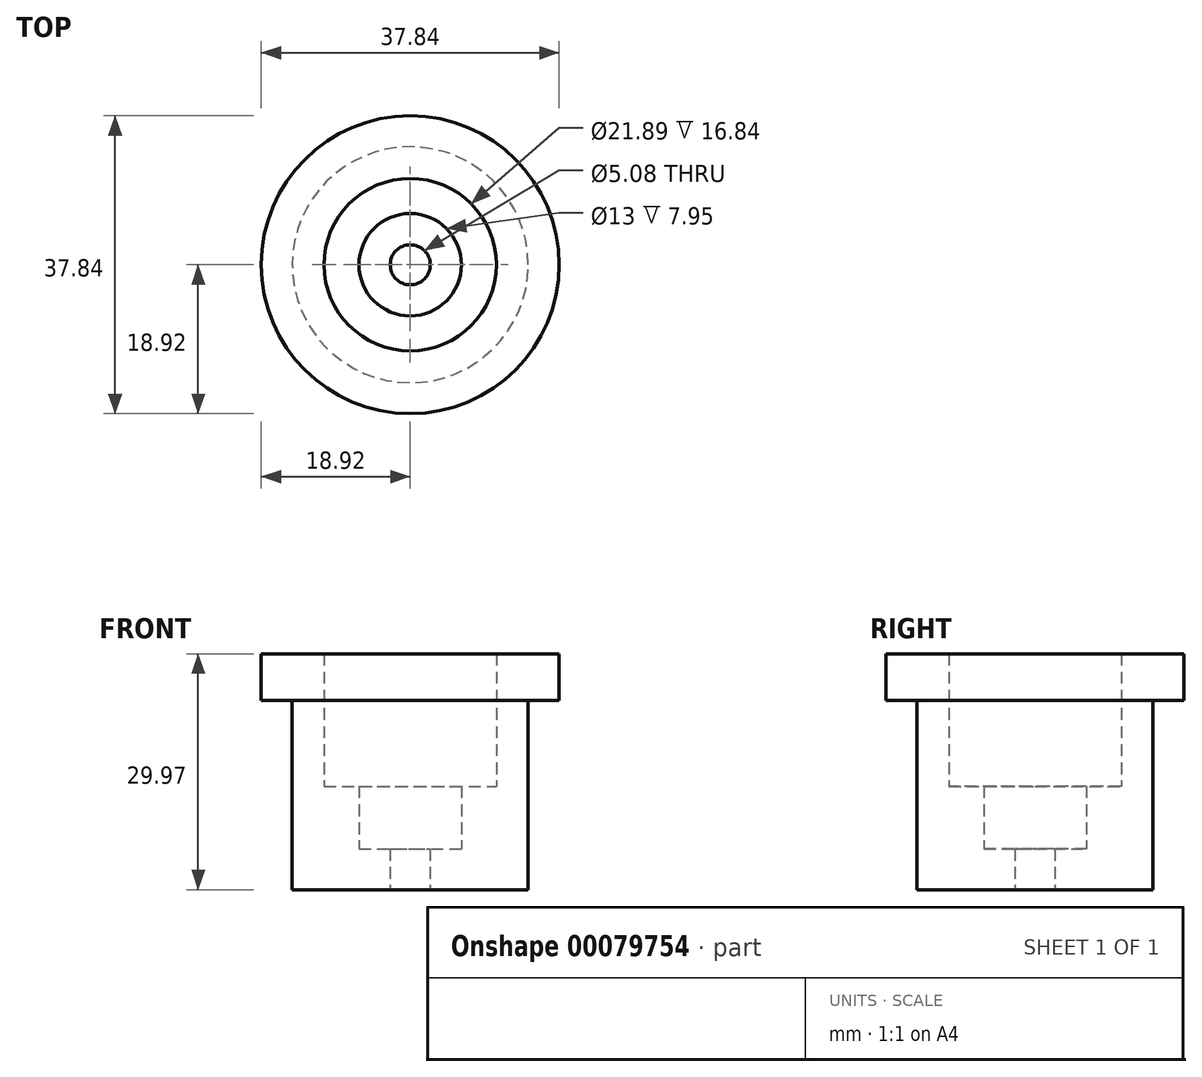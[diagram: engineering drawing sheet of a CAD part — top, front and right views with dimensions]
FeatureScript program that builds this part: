
annotation { "Feature Type Name" : "Feature", "Feature Type Description" : "" }
export const myFeature = defineFeature(function(context is Context, id is Id, definition is map)
    precondition{}
    {
        {
            var Q0;
            Q0=qCreatedBy(makeId("Front.planeOp"),FACE);
            var sketch = newSketch(context, id + "F0", { "sketchPlane" : qUnion([Q0])});
            skLineSegment(sketch, "E0.bottom", {"start": v(0, 0) * mm, "end": v(0, 0) * mm});
            skLineSegment(sketch, "E0.top", {"start": v(0, 29.97) * mm, "end": v(0, 29.97) * mm});
            skLineSegment(sketch, "E1", {"start": v(-10.95, 29.97) * mm, "end": v(-18.92, 29.97) * mm});
            skLineSegment(sketch, "E2", {"start": v(-18.92, 29.97) * mm, "end": v(-18.92, 24.03) * mm});
            skLineSegment(sketch, "E3", {"start": v(-18.92, 24.03) * mm, "end": v(-14.99, 24.03) * mm});
            skLineSegment(sketch, "E4", {"start": v(-14.99, 24.03) * mm, "end": v(-14.99, 0) * mm});
            skLineSegment(sketch, "E5", {"start": v(-14.99, 0) * mm, "end": v(-2.54, 0) * mm});
            skLineSegment(sketch, "E6", {"start": v(0, 0) * mm, "end": v(0, 39.52) * mm});
            skLineSegment(sketch, "E7", {"start": v(-10.95, 29.97) * mm, "end": v(-10.95, 13.13) * mm});
            skLineSegment(sketch, "E8", {"start": v(-10.95, 13.13) * mm, "end": v(-6.5, 13.13) * mm});
            skLineSegment(sketch, "E9", {"start": v(-6.5, 13.13) * mm, "end": v(-6.5, 5.18) * mm});
            skLineSegment(sketch, "E10", {"start": v(-6.5, 5.18) * mm, "end": v(-2.54, 5.18) * mm});
            skLineSegment(sketch, "E11", {"start": v(-2.54, 5.18) * mm, "end": v(-2.54, 0) * mm});
            skSolve(sketch);
        }
        {
            var Q0;
            Q0 = qSketchRegion(id + "F0", true);
            var Q1;
            Q1=sQuery(id+"F0.wireOp",EDGE,"E6");
            revolve(context, id + "F1", {"entities" : qUnion([Q0]), "axis" : qUnion([Q1]), "revolveType" : RevolveType.FULL});
        }
    });
